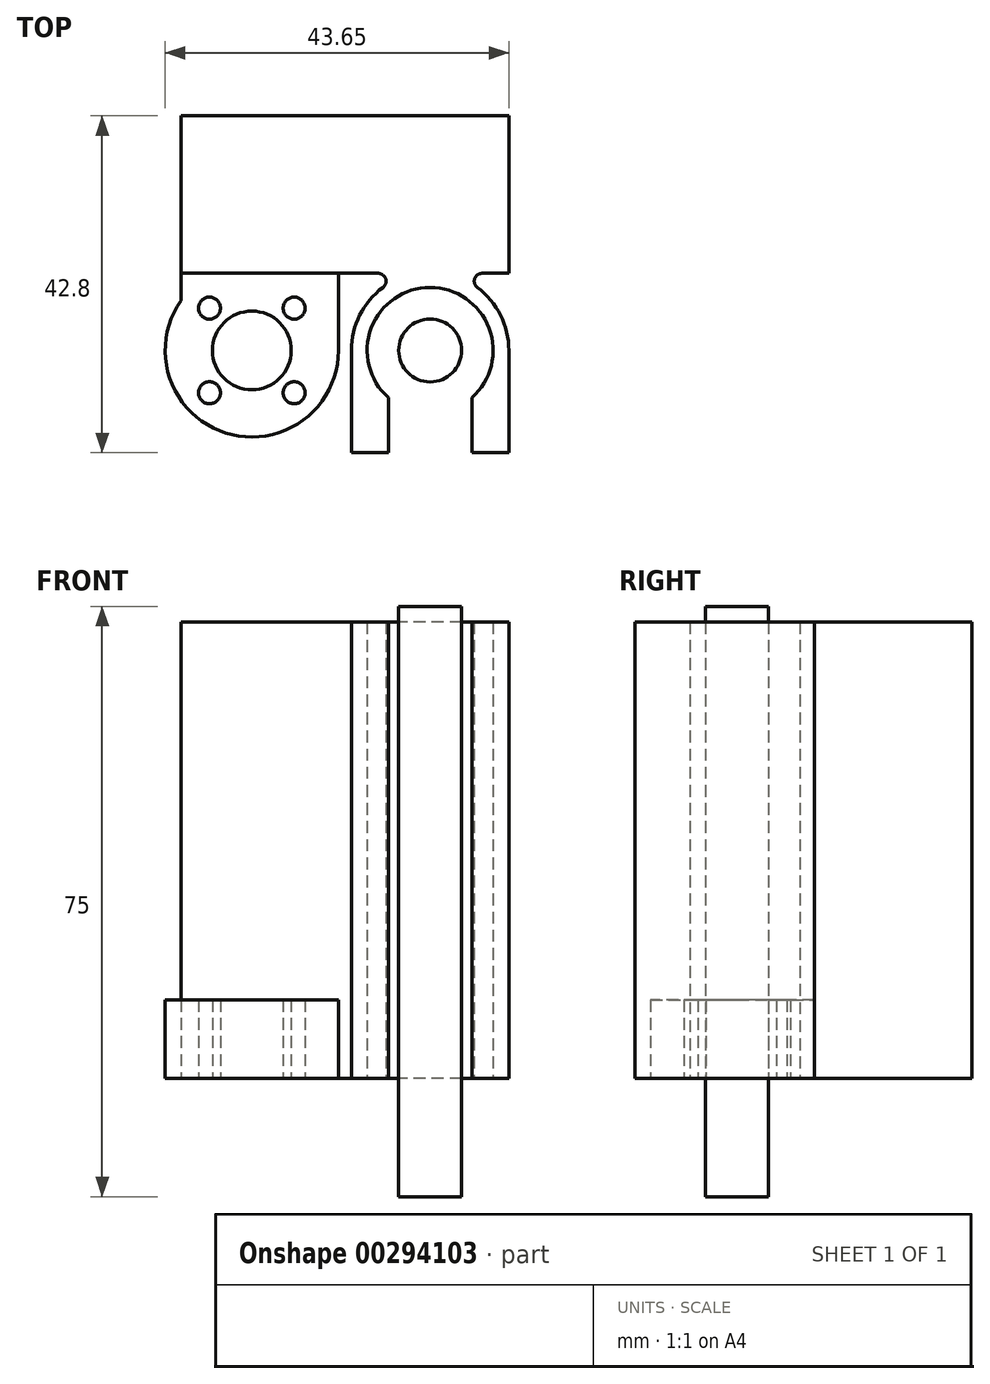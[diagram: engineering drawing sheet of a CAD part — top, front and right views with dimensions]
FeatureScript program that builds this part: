
annotation { "Feature Type Name" : "Feature", "Feature Type Description" : "" }
export const myFeature = defineFeature(function(context is Context, id is Id, definition is map)
    precondition{}
    {
        {
            var Q0;
            Q0=qCreatedBy(makeId("Top.planeOp"),FACE);
            var sketch = newSketch(context, id + "F0", { "sketchPlane" : qUnion([Q0])});
            skCircle(sketch, "E0", {"center": v(0, 0) * mm, "radius": 5 * mm});
            skArc(sketch, "E1", {"start": v(-9, 6.32) * mm, "mid": v(-3.32, -10.49) * mm, "end": v(11, 0) * mm});
            skLineSegment(sketch, "E2.left", {"start": v(12.65, -13) * mm, "end": v(12.65, 0) * mm});
            skLineSegment(sketch, "E2.right", {"start": v(32.65, -13) * mm, "end": v(32.65, 0) * mm});
            skArc(sketch, "E3", {"start": v(32.65, 0) * mm, "mid": v(31.6, 4.47) * mm, "end": v(28.65, 8) * mm});
            skLineSegment(sketch, "E4.bottom", {"start": v(-9, 29.8) * mm, "end": v(32.65, 29.8) * mm});
            skLineSegment(sketch, "E4.right", {"start": v(32.65, 29.8) * mm, "end": v(32.65, 9.8) * mm});
            skLineSegment(sketch, "E5", {"start": v(-9, 29.8) * mm, "end": v(-9, 6.32) * mm});
            skLineSegment(sketch, "E6", {"start": v(11, 0) * mm, "end": v(11, 9.8) * mm});
            skLineSegment(sketch, "E7.trimOffspring", {"start": v(29.25, 9.8) * mm, "end": v(32.65, 9.8) * mm});
            skArc(sketch, "E8.filletArc", {"start": v(29.25, 9.8) * mm, "mid": v(28.3, 9.12) * mm, "end": v(28.65, 8) * mm});
            skArc(sketch, "E9", {"start": v(16.65, 8) * mm, "mid": v(13.7, 4.47) * mm, "end": v(12.65, 0) * mm});
            skArc(sketch, "E10.filletArc", {"start": v(16.65, 8) * mm, "mid": v(17, 9.12) * mm, "end": v(16.05, 9.8) * mm});
            skLineSegment(sketch, "E11.left", {"start": v(17.35, -13) * mm, "end": v(17.35, -6) * mm});
            skLineSegment(sketch, "E11.right", {"start": v(27.95, -13) * mm, "end": v(27.95, -6) * mm});
            skArc(sketch, "E12", {"start": v(27.95, -6) * mm, "mid": v(22.65, 8) * mm, "end": v(17.35, -6) * mm});
            skLineSegment(sketch, "E13", {"start": v(22.65, 8) * mm, "end": v(22.65, -13) * mm, "construction": true});
            skLineSegment(sketch, "E14", {"start": v(12.65, -13) * mm, "end": v(17.35, -13) * mm});
            skLineSegment(sketch, "E15", {"start": v(27.95, -13) * mm, "end": v(32.65, -13) * mm});
            skLineSegment(sketch, "E16", {"start": v(16.05, 9.8) * mm, "end": v(-9, 9.8) * mm});
            skCircle(sketch, "E17", {"center": v(22.65, 0) * mm, "radius": 4 * mm});
            skLineSegment(sketch, "E18", {"start": v(-7.78, 7.78) * mm, "end": v(7.78, -7.78) * mm, "construction": true});
            skLineSegment(sketch, "E19", {"start": v(-7.78, -7.78) * mm, "end": v(7.78, 7.78) * mm, "construction": true});
            skCircle(sketch, "E20", {"center": v(-5.37, 5.37) * mm, "radius": 1.4 * mm});
            skCircle(sketch, "E21", {"center": v(5.37, 5.37) * mm, "radius": 1.4 * mm});
            skCircle(sketch, "E22", {"center": v(5.37, -5.37) * mm, "radius": 1.4 * mm});
            skCircle(sketch, "E23", {"center": v(-5.37, -5.37) * mm, "radius": 1.4 * mm});
            skCircle(sketch, "E24", {"center": v(0, 0) * mm, "radius": 7.6 * mm, "construction": true});
            skLineSegment(sketch, "E25", {"start": v(0, 0) * mm, "end": v(22.65, 0) * mm, "construction": true});
            skSolve(sketch);
        }
        {
            var Q0;
            Q0=makeQuery(id+"F0.imprint","IMPRINT",FACE,{"disambiguationData":[TD([[makeQuery(id+"F0.imprint","IMPRINT",EDGE,{"derivedFrom":sQuery(id+"F0.wireOp",EDGE,"E2.left")}),-1.0]])]});
            var Q1;
            Q1=makeQuery(id+"F0.imprint","IMPRINT",FACE,{"disambiguationData":[TD([[makeQuery(id+"F0.imprint","IMPRINT",EDGE,{"derivedFrom":sQuery(id+"F0.wireOp",EDGE,"E0")}),-1.0]])]});
            extrude(context, id + "F1", {"entities" : qUnion([Q0, Q1]), "depth" : 10 * mm});
        }
        {
            var Q0;
            Q0=makeQuery(id+"F0.imprint","IMPRINT",FACE,{"disambiguationData":[TD([[makeQuery(id+"F0.imprint","IMPRINT",EDGE,{"derivedFrom":sQuery(id+"F0.wireOp",EDGE,"E2.left")}),-1.0]])]});
            extrude(context, id + "F2", {"entities" : qUnion([Q0]), "operationType" : NewBodyOperationType.ADD, "depth" : 58 * mm});
        }
        {
            var Q0;
            Q0=makeQuery(id+"F0.imprint","IMPRINT",FACE,{"disambiguationData":[TD([[makeQuery(id+"F0.imprint","IMPRINT",EDGE,{"derivedFrom":sQuery(id+"F0.wireOp",EDGE,"E17")}),1.0]])]});
            extrude(context, id + "F3", {"entities" : qUnion([Q0]), "depth" : (120 / 2) * mm, "hasSecondDirection" : true, "secondDirectionOppositeDirection" : true, "secondDirectionDepth" : 15 * mm});
        }
    });
